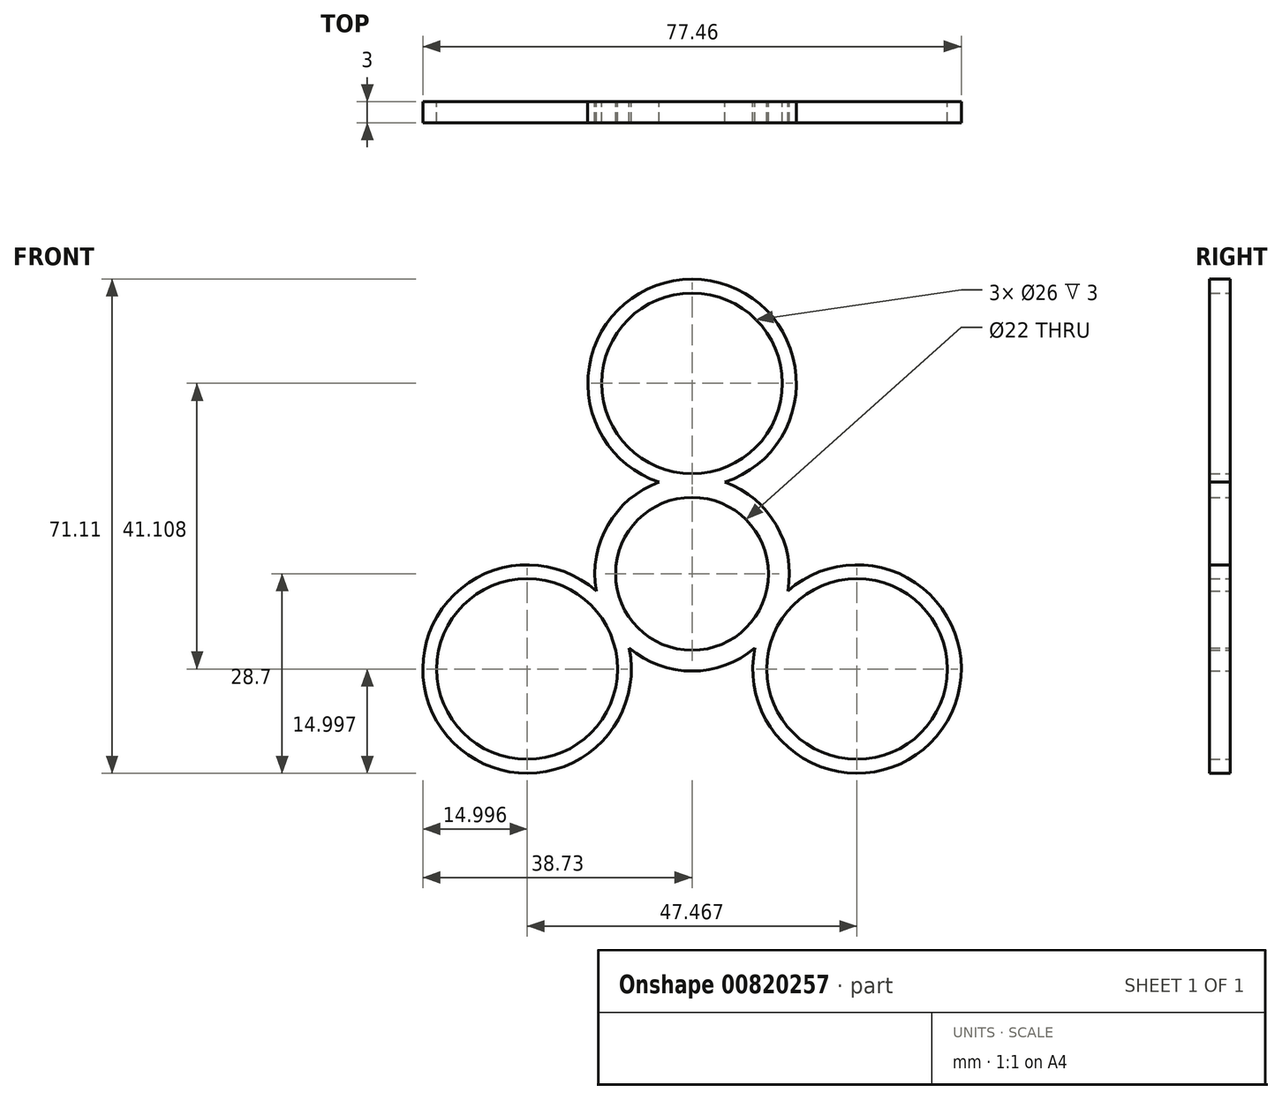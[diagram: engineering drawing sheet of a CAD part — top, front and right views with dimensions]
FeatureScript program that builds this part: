
annotation { "Feature Type Name" : "Feature", "Feature Type Description" : "" }
export const myFeature = defineFeature(function(context is Context, id is Id, definition is map)
    precondition{}
    {
        {
            var Q0;
            Q0=qCreatedBy(makeId("Front.planeOp"),FACE);
            var sketch = newSketch(context, id + "F0", { "sketchPlane" : qUnion([Q0])});
            skCircle(sketch, "E0", {"center": v(0, 0) * mm, "radius": 11 * mm});
            skCircle(sketch, "E1", {"center": v(0, 27.4) * mm, "radius": 13 * mm});
            skCircle(sketch, "E2.1.0", {"center": v(23.73, -13.7) * mm, "radius": 13 * mm});
            skCircle(sketch, "E2.2.0", {"center": v(-23.73, -13.7) * mm, "radius": 13 * mm});
            skLineSegment(sketch, "E2.anchor1", {"start": v(0, 11) * mm, "end": v(0, 12.4) * mm, "construction": true});
            skLineSegment(sketch, "E2.anchor2", {"start": v(-12.12, -7) * mm, "end": v(-12.48, -7.2) * mm, "construction": true});
            skArc(sketch, "E3", {"start": v(-4.86, 13.21) * mm, "mid": v(-4.85, 13.18) * mm, "end": v(-4.84, 13.14) * mm});
            skPoint(sketch, "E3.centerSnap0", {"position": v(0, 13.7) * mm});
            skArc(sketch, "E4.1.0", {"start": v(-13.8, -2.38) * mm, "mid": v(-13.83, -2.4) * mm, "end": v(-13.87, -2.4) * mm});
            skArc(sketch, "E4.2.0", {"start": v(8.96, -10.76) * mm, "mid": v(8.99, -10.78) * mm, "end": v(9.01, -10.81) * mm});
            skArc(sketch, "E5", {"start": v(4.74, 13.17) * mm, "mid": v(0, 42.4) * mm, "end": v(-4.74, 13.17) * mm});
            skArc(sketch, "E6.1.0", {"start": v(-13.78, -2.48) * mm, "mid": v(-36.72, -21.2) * mm, "end": v(-9.04, -10.7) * mm});
            skArc(sketch, "E6.2.0", {"start": v(9.04, -10.7) * mm, "mid": v(36.72, -21.2) * mm, "end": v(13.78, -2.48) * mm});
            skArc(sketch, "E7", {"start": v(-9.04, -10.7) * mm, "mid": v(0, -14) * mm, "end": v(9.04, -10.7) * mm});
            skArc(sketch, "E8.trimOffspring", {"start": v(-9.01, -10.81) * mm, "mid": v(-8.99, -10.78) * mm, "end": v(-8.96, -10.76) * mm});
            skArc(sketch, "E9.trimOffspring", {"start": v(13.87, -2.4) * mm, "mid": v(13.83, -2.4) * mm, "end": v(13.8, -2.38) * mm});
            skArc(sketch, "E10.trimOffspring", {"start": v(13.78, -2.48) * mm, "mid": v(12.12, 7) * mm, "end": v(4.74, 13.17) * mm});
            skLineSegment(sketch, "E11.trimOffspring", {"start": v(0, 14.4) * mm, "end": v(0, 27.4) * mm, "construction": true});
            skArc(sketch, "E12.trimOffspring", {"start": v(-4.74, 13.17) * mm, "mid": v(-12.12, 7) * mm, "end": v(-13.78, -2.48) * mm});
            skArc(sketch, "E13.trimOffspring", {"start": v(4.84, 13.14) * mm, "mid": v(4.85, 13.18) * mm, "end": v(4.86, 13.21) * mm});
            skSolve(sketch);
        }
        {
            var Q0;
            Q0=makeQuery(id+"F0.imprint","IMPRINT",FACE,{"disambiguationData":[TD([[makeQuery(id+"F0.imprint","IMPRINT",EDGE,{"derivedFrom":sQuery(id+"F0.wireOp",EDGE,"E0")}),-1.0]])]});
            extrude(context, id + "F1", {"entities" : qUnion([Q0]), "depth" : 3 * mm, "offsetDistance" : 25 * mm});
        }
    });
